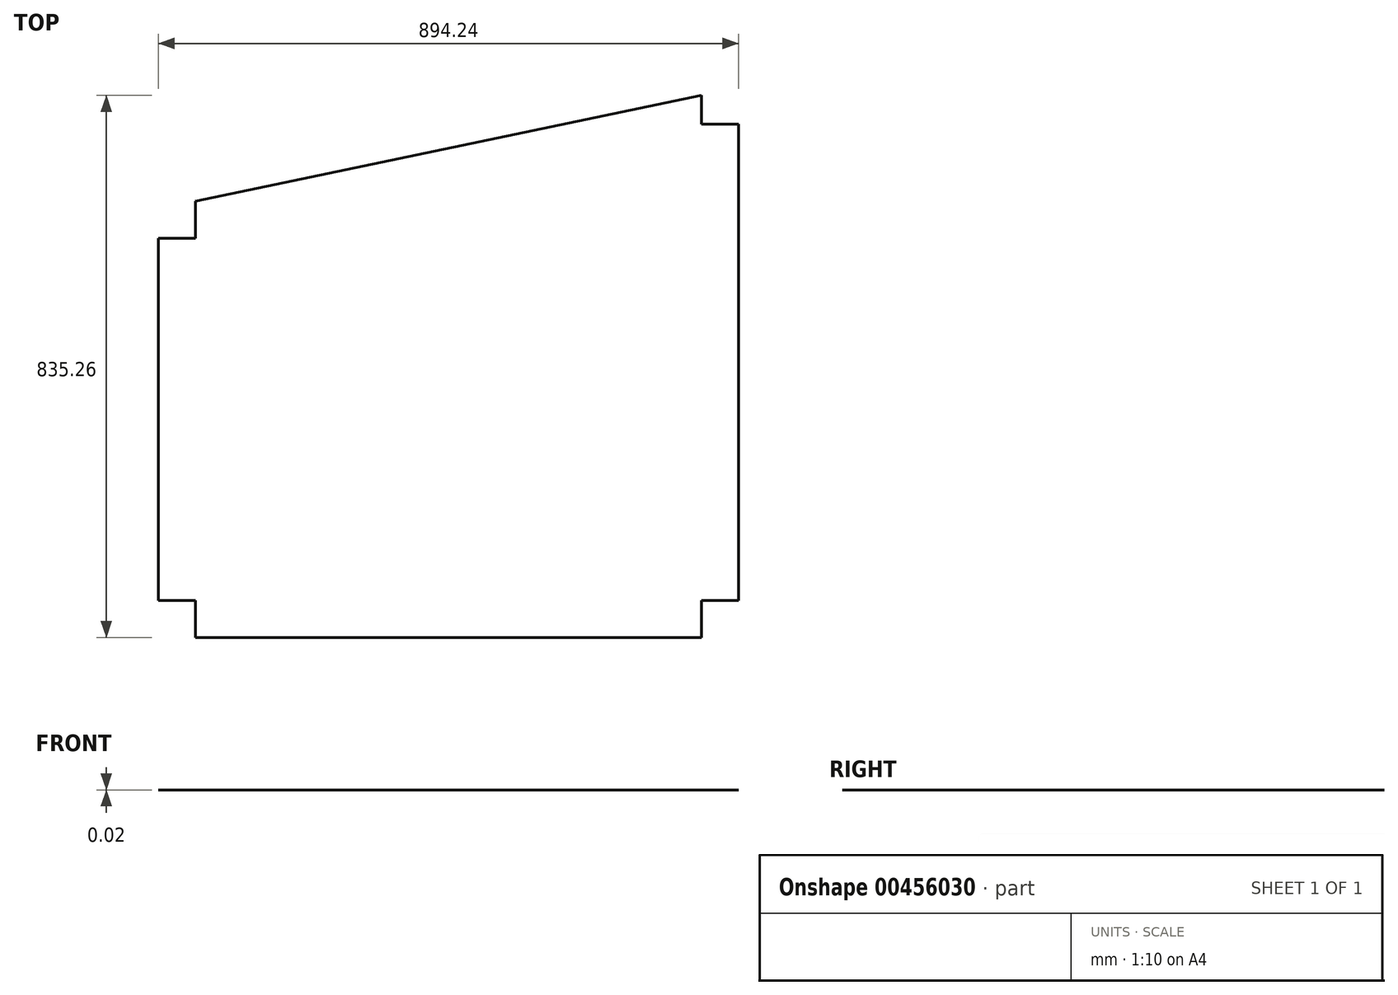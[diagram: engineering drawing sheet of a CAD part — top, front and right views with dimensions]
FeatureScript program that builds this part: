
annotation { "Feature Type Name" : "Feature", "Feature Type Description" : "" }
export const myFeature = defineFeature(function(context is Context, id is Id, definition is map)
    precondition{}
    {
        {
            var Q0;
            Q0=qCreatedBy(makeId("Top.planeOp"),FACE);
            var sketch = newSketch(context, id + "F0", { "sketchPlane" : qUnion([Q0])});
            skLineSegment(sketch, "E0", {"start": v(57.15, 0) * mm, "end": v(831.85, 0) * mm});
            skLineSegment(sketch, "E1", {"start": v(837.1, 835.26) * mm, "end": v(57.15, 672.34) * mm});
            skLineSegment(sketch, "E2.top", {"start": v(0, 57.15) * mm, "end": v(57.15, 57.15) * mm});
            skLineSegment(sketch, "E3.right", {"start": v(837.1, 835.26) * mm, "end": v(837.1, 790.77) * mm});
            skLineSegment(sketch, "E4", {"start": v(837.1, 790.77) * mm, "end": v(894.24, 790.77) * mm});
            skLineSegment(sketch, "E5", {"start": v(57.15, 672.34) * mm, "end": v(57.15, 615.19) * mm});
            skLineSegment(sketch, "E6", {"start": v(57.15, 615.19) * mm, "end": v(0, 615.19) * mm});
            skPoint(sketch, "E7.orphan", {"position": v(0, 660.4) * mm});
            skLineSegment(sketch, "E8", {"start": v(57.15, 57.15) * mm, "end": v(57.15, 0) * mm});
            skLineSegment(sketch, "E9", {"start": v(837.1, 0) * mm, "end": v(831.85, 0) * mm});
            skLineSegment(sketch, "E10.top", {"start": v(894.24, 57.15) * mm, "end": v(837.1, 57.15) * mm});
            skLineSegment(sketch, "E10.right", {"start": v(837.1, 0) * mm, "end": v(837.1, 57.15) * mm});
            skPoint(sketch, "E10.bottom.start.orphan", {"position": v(894.24, 0) * mm});
            skLineSegment(sketch, "E11", {"start": v(0, 615.19) * mm, "end": v(0, 57.15) * mm});
            skLineSegment(sketch, "E12", {"start": v(894.24, 790.77) * mm, "end": v(894.24, 57.15) * mm});
            skSolve(sketch);
        }
        {
            var Q0;
            Q0=makeQuery(id+"F0.imprint","IMPRINT",FACE,{"disambiguationData":[TD([[makeQuery(id+"F0.imprint","IMPRINT",EDGE,{"derivedFrom":sQuery(id+"F0.wireOp",EDGE,"E0")}),1.0]])]});
            extrude(context, id + "F1", {"entities" : qUnion([Q0]), "depth" : 1 / 50.8 * mm});
        }
    });
